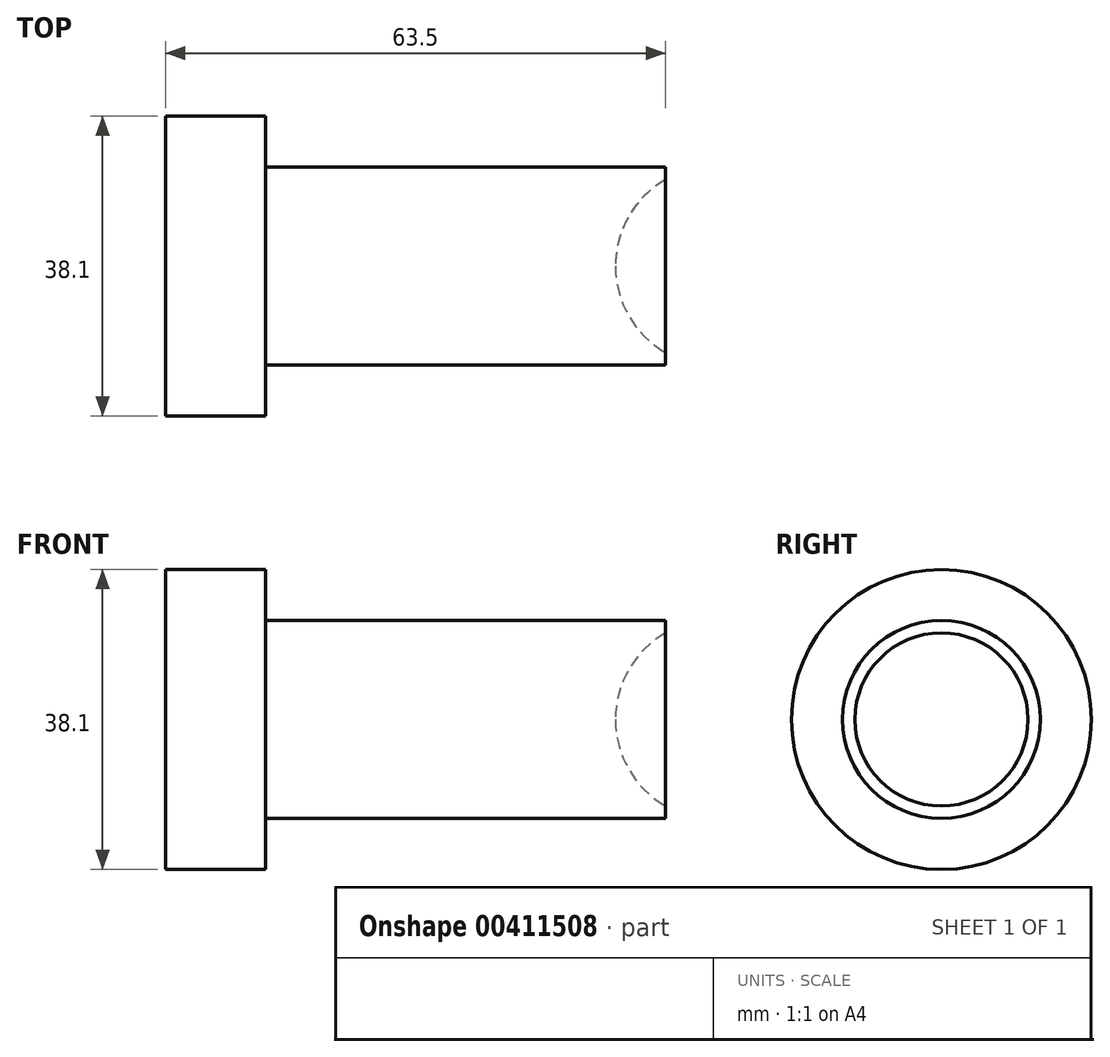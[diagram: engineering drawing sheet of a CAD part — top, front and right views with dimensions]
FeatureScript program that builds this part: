
annotation { "Feature Type Name" : "Feature", "Feature Type Description" : "" }
export const myFeature = defineFeature(function(context is Context, id is Id, definition is map)
    precondition{}
    {
        {
            var Q0;
            Q0=qCreatedBy(makeId("Right.planeOp"),FACE);
            var sketch = newSketch(context, id + "F0", { "sketchPlane" : qUnion([Q0])});
            skCircle(sketch, "E0", {"center": v(0, 0) * mm, "radius": 19.05 * mm});
            skSolve(sketch);
        }
        {
            var Q0;
            Q0=qSketchRegion(id+"F0",true);
            extrude(context, id + "F1", {"entities" : qUnion([Q0]), "depth" : 12.7 * mm});
        }
        {
            var Q0;
            Q0=makeQuery(id+"F1.opExtrude","CAP_FACE",FACE,{"disambiguationData":[OSD([sQuery(id+"F0.wireOp",EDGE,"E0")])],"isStart":false});
            var sketch = newSketch(context, id + "F2", { "sketchPlane" : qUnion([Q0])});
            skCircle(sketch, "E1", {"center": v(0, 0) * mm, "radius": 12.57 * mm});
            skSolve(sketch);
        }
        {
            var Q0;
            Q0=qSketchRegion(id+"F2",true);
            extrude(context, id + "F3", {"entities" : qUnion([Q0]), "operationType" : NewBodyOperationType.ADD, "depth" : 50.8 * mm});
        }
        {
            var Q0;
            Q0=qCreatedBy(makeId("Top.planeOp"),FACE);
            var sketch = newSketch(context, id + "F4", { "sketchPlane" : qUnion([Q0])});
            skArc(sketch, "E2", {"start": v(63.5, 11) * mm, "mid": v(58.85, 6.35) * mm, "end": v(57.15, 0) * mm});
            skLineSegment(sketch, "E3", {"start": v(63.5, 0) * mm, "end": v(57.15, 0) * mm});
            skLineSegment(sketch, "E4", {"start": v(63.5, 0) * mm, "end": v(63.5, 11) * mm});
            skSolve(sketch);
        }
        {
            var Q0;
            Q0=qCreatedBy(makeId("Top.planeOp"),FACE);
            var sketch = newSketch(context, id + "F5", { "sketchPlane" : qUnion([Q0])});
            skLineSegment(sketch, "E5", {"start": v(92.71, 0) * mm, "end": v(43.19, 0) * mm, "construction": true});
            skSolve(sketch);
        }
        {
            var Q0;
            Q0=qSketchRegion(id+"F4",true);
            var Q1;
            Q1=sQuery(id+"F5.wireOp",EDGE,"E5");
            revolve(context, id + "F6", {"operationType" : NewBodyOperationType.REMOVE, "entities" : qUnion([Q0]), "axis" : qUnion([Q1]), "revolveType" : RevolveType.FULL, "oppositeDirection" : true});
        }
    });
